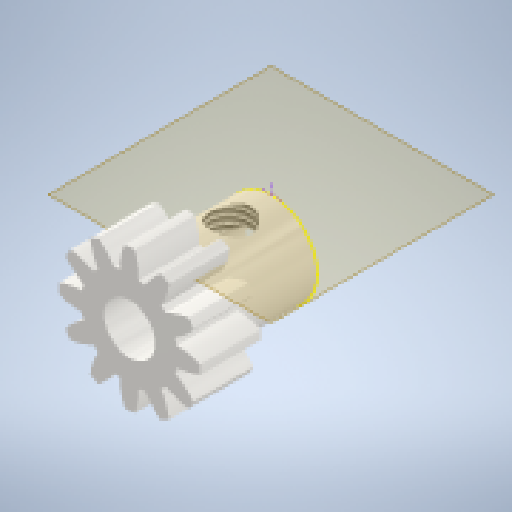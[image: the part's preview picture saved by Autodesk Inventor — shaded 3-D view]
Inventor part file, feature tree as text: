
AUTODESK INVENTOR PART (.ipt)
format: ipt  version: 2024 (Build 280153000, 153)  size: 289,280 bytes
history: native  units: mm (DEFAULTED — no unit token found)
features: sketch x5, other x4, plane x3, extrude x2, hole x2, thread x1
ambient origin geometry x8: Origin, YZ Plane, XZ Plane, XY Plane, X Axis, Y Axis, Z Axis, Center Point
bodies: Solid1 (feature_tree)
feature tree (17):
  extrude  "Extrusion1"  Depth=6.0mm TaperAngle=0.0deg
  plane  "Work Plane2"
  plane  "Work Plane8"
  plane  "Work Plane9"
  other  "平歯車"
  extrude  "押し出し2"  Depth=2.0mm
  hole  "穴1"  [1 undecoded]
  sketch  "スケッチ5"
  other  "作業平面11"
  hole  "穴2"  [1 undecoded]
  thread  "ねじ1"
  sketch  "Sketch1"  dims[d0=14.0mm d1=6.0mm d2=0.0mm d3=12.0mm d4=10.0mm d5=0.0mm d16=34.5mm d17=0.0mm d34=15.0deg d39=0.0mm d41=0.0mm d43=34.5mm d46=34.5mm d47=0.0mm d48=0.0mm d49=9.0mm d50=8.0mm d51=0.0mm d52=5.0mm d53=6.0mm d54=4.0mm d55=2.0mm d56=90.0deg d57=8.0mm d58=20.594885mm d59=4.0mm d60=4.0mm d61=6.0mm d62=4.0mm d63=2.0mm d64=90.0deg d65=4.0mm d66=20.594885mm d67=3.0mm d68=0.0mm]
  other  "Srf1"
  sketch  "スケッチ3"
  sketch  "スケッチ4"
  sketch  "スケッチ6"
  other  "ピッチ円直径"
note: 2 required parameter values undecoded (feature->parameter linkage not recoverable at this tier; creation-order binding heuristic only, values carry confidence <= 0.55)
